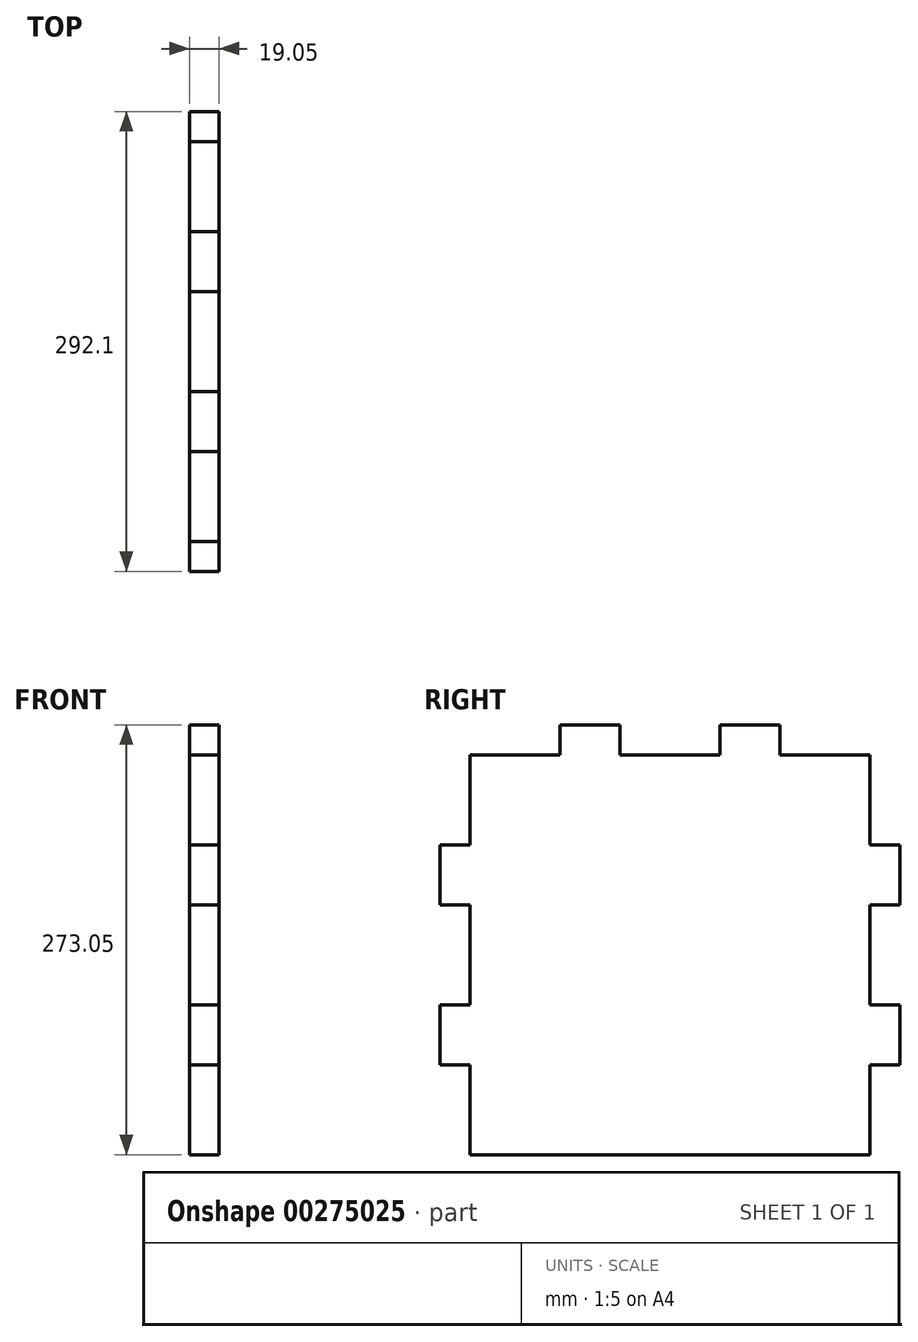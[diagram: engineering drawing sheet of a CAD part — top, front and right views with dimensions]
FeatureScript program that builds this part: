
annotation { "Feature Type Name" : "Feature", "Feature Type Description" : "" }
export const myFeature = defineFeature(function(context is Context, id is Id, definition is map)
    precondition{}
    {
        {
            var Q0;
            Q0=qCreatedBy(makeId("Top.planeOp"),FACE);
            var sketch = newSketch(context, id + "F0", { "sketchPlane" : qUnion([Q0])});
            skLineSegment(sketch, "E0.bottom", {"start": v(57.29, 129.7) * mm, "end": v(38.24, 129.7) * mm});
            skLineSegment(sketch, "E0.top", {"start": v(57.29, -124.3) * mm, "end": v(38.24, -124.3) * mm});
            skLineSegment(sketch, "E0.left", {"start": v(57.29, 129.7) * mm, "end": v(57.29, -124.3) * mm});
            skLineSegment(sketch, "E0.right", {"start": v(38.24, 129.7) * mm, "end": v(38.24, -124.3) * mm});
            skSolve(sketch);
        }
        {
            var Q0;
            Q0 = qSketchRegion(id + "F0", true);
            extrude(context, id + "F1", {"entities" : qUnion([Q0]), "depth" : 254 * mm});
        }
        {
            var Q0;
            Q0=makeQuery(id+"F1.opExtrude","SWEPT_FACE",FACE,{"disambiguationData":[OSD([sQuery(id+"F0.wireOp",EDGE,"E0.top")])]});
            var sketch = newSketch(context, id + "F2", { "sketchPlane" : qUnion([Q0])});
            skLineSegment(sketch, "E1.bottom", {"start": v(38.24, 57.15) * mm, "end": v(57.29, 57.15) * mm});
            skLineSegment(sketch, "E1.top", {"start": v(38.24, 95.25) * mm, "end": v(57.29, 95.25) * mm});
            skLineSegment(sketch, "E1.left", {"start": v(38.24, 57.15) * mm, "end": v(38.24, 95.25) * mm});
            skLineSegment(sketch, "E1.right", {"start": v(57.29, 57.15) * mm, "end": v(57.29, 95.25) * mm});
            skLineSegment(sketch, "E2.bottom", {"start": v(38.24, 158.75) * mm, "end": v(57.29, 158.75) * mm});
            skLineSegment(sketch, "E2.top", {"start": v(38.24, 196.85) * mm, "end": v(57.29, 196.85) * mm});
            skLineSegment(sketch, "E2.left", {"start": v(38.24, 158.75) * mm, "end": v(38.24, 196.85) * mm});
            skLineSegment(sketch, "E2.right", {"start": v(57.29, 158.75) * mm, "end": v(57.29, 196.85) * mm});
            skSolve(sketch);
        }
        {
            var Q0;
            Q0 = qSketchRegion(id + "F2", true);
            extrude(context, id + "F3", {"entities" : qUnion([Q0]), "operationType" : NewBodyOperationType.ADD, "depth" : 19.05 * mm});
        }
        {
            var Q0;
            Q0=makeQuery(id+"F1.opExtrude","CAP_FACE",FACE,{"disambiguationData":[OSD([sQuery(id+"F0.wireOp",EDGE,"E0.bottom"),sQuery(id+"F0.wireOp",EDGE,"E0.top"),sQuery(id+"F0.wireOp",EDGE,"E0.left"),sQuery(id+"F0.wireOp",EDGE,"E0.right")])],"isStart":false});
            var sketch = newSketch(context, id + "F4", { "sketchPlane" : qUnion([Q0])});
            skLineSegment(sketch, "E3.bottom", {"start": v(38.24, 72.55) * mm, "end": v(57.29, 72.55) * mm});
            skLineSegment(sketch, "E3.top", {"start": v(38.24, 34.45) * mm, "end": v(57.29, 34.45) * mm});
            skLineSegment(sketch, "E3.left", {"start": v(38.24, 72.55) * mm, "end": v(38.24, 34.45) * mm});
            skLineSegment(sketch, "E3.right", {"start": v(57.29, 72.55) * mm, "end": v(57.29, 34.45) * mm});
            skLineSegment(sketch, "E4.bottom", {"start": v(38.24, -29.05) * mm, "end": v(57.29, -29.05) * mm});
            skLineSegment(sketch, "E4.top", {"start": v(38.24, -67.15) * mm, "end": v(57.29, -67.15) * mm});
            skLineSegment(sketch, "E4.left", {"start": v(38.24, -29.05) * mm, "end": v(38.24, -67.15) * mm});
            skLineSegment(sketch, "E4.right", {"start": v(57.29, -29.05) * mm, "end": v(57.29, -67.15) * mm});
            skSolve(sketch);
        }
        {
            var Q0;
            Q0 = qSketchRegion(id + "F4", true);
            extrude(context, id + "F5", {"entities" : qUnion([Q0]), "operationType" : NewBodyOperationType.ADD, "depth" : 19.05 * mm});
        }
        {
            var Q0;
            Q0=makeQuery(id+"F1.opExtrude","SWEPT_FACE",FACE,{"disambiguationData":[OSD([sQuery(id+"F0.wireOp",EDGE,"E0.bottom")])]});
            var sketch = newSketch(context, id + "F6", { "sketchPlane" : qUnion([Q0])});
            skLineSegment(sketch, "E5.bottom", {"start": v(-57.29, 57.15) * mm, "end": v(-38.24, 57.15) * mm});
            skLineSegment(sketch, "E5.top", {"start": v(-57.29, 95.25) * mm, "end": v(-38.24, 95.25) * mm});
            skLineSegment(sketch, "E5.left", {"start": v(-57.29, 57.15) * mm, "end": v(-57.29, 95.25) * mm});
            skLineSegment(sketch, "E5.right", {"start": v(-38.24, 57.15) * mm, "end": v(-38.24, 95.25) * mm});
            skLineSegment(sketch, "E6.bottom", {"start": v(-57.29, 158.75) * mm, "end": v(-38.24, 158.75) * mm});
            skLineSegment(sketch, "E6.top", {"start": v(-57.29, 196.85) * mm, "end": v(-38.24, 196.85) * mm});
            skLineSegment(sketch, "E6.left", {"start": v(-57.29, 158.75) * mm, "end": v(-57.29, 196.85) * mm});
            skLineSegment(sketch, "E6.right", {"start": v(-38.24, 158.75) * mm, "end": v(-38.24, 196.85) * mm});
            skSolve(sketch);
        }
        {
            var Q0;
            Q0 = qSketchRegion(id + "F6", true);
            extrude(context, id + "F7", {"entities" : qUnion([Q0]), "operationType" : NewBodyOperationType.ADD, "depth" : 19.05 * mm});
        }
    });
